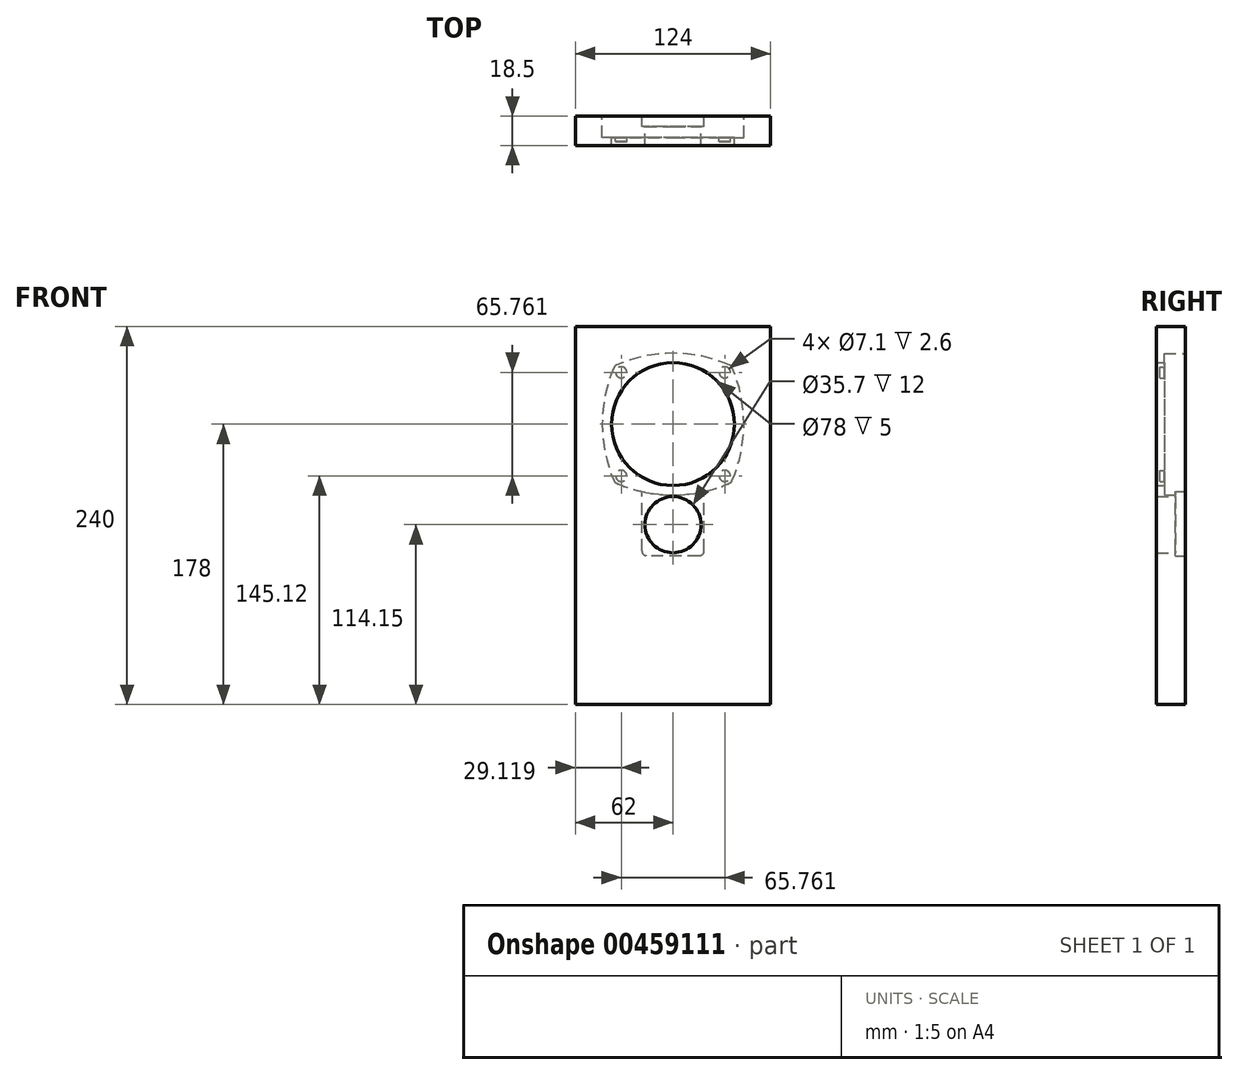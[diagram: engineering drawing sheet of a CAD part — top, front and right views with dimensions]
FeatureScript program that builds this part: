
annotation { "Feature Type Name" : "Feature", "Feature Type Description" : "" }
export const myFeature = defineFeature(function(context is Context, id is Id, definition is map)
    precondition{}
    {
        {
            var Q0;
            Q0=qCreatedBy(makeId("Front.planeOp"),FACE);
            var sketch = newSketch(context, id + "F0", { "sketchPlane" : qUnion([Q0])});
            skLineSegment(sketch, "E0.bottom", {"start": v(0, 0) * mm, "end": v(124, 0) * mm});
            skLineSegment(sketch, "E0.top", {"start": v(0, -240) * mm, "end": v(124, -240) * mm});
            skLineSegment(sketch, "E0.left", {"start": v(0, 0) * mm, "end": v(0, -240) * mm});
            skLineSegment(sketch, "E0.right", {"start": v(124, 0) * mm, "end": v(124, -240) * mm});
            skSolve(sketch);
        }
        {
            var Q0;
            Q0 = qSketchRegion(id + "F0", true);
            extrude(context, id + "F1", {"entities" : qUnion([Q0]), "depth" : 18.5 * mm});
        }
        {
            var Q0;
            Q0=makeQuery(id+"F1.opExtrude","CAP_FACE",FACE,{"disambiguationData":[OSD([sQuery(id+"F0.wireOp",EDGE,"E0.bottom"),sQuery(id+"F0.wireOp",EDGE,"E0.top"),sQuery(id+"F0.wireOp",EDGE,"E0.left"),sQuery(id+"F0.wireOp",EDGE,"E0.right")])],"isStart":true});
            var sketch = newSketch(context, id + "F2", { "sketchPlane" : qUnion([Q0])});
            skCircle(sketch, "E1", {"center": v(-62, -62) * mm, "radius": 39 * mm});
            skLineSegment(sketch, "E2", {"start": v(-62, 0) * mm, "end": v(-62, -240) * mm, "construction": true});
            skCircle(sketch, "E3", {"center": v(-62, -125.85) * mm, "radius": 17.85 * mm});
            skSolve(sketch);
        }
        {
            var Q0;
            Q0 = qSketchRegion(id + "F2", true);
            extrude(context, id + "F3", {"entities" : qUnion([Q0]), "operationType" : NewBodyOperationType.REMOVE, "endBound" : BoundingType.THROUGH_ALL, "oppositeDirection" : true, "depth" : 25.4 * mm});
        }
        {
            var Q0;
            Q0=makeQuery(id+"F2.imprint","IMPRINT",FACE,{"disambiguationData":[TD([[makeQuery(id+"F2.imprint","IMPRINT",EDGE,{"derivedFrom":sQuery(id+"F2.wireOp",EDGE,"E1")}),-1.0]])]});
            var sketch = newSketch(context, id + "F4", { "sketchPlane" : qUnion([Q0])});
            skLineSegment(sketch, "E4", {"start": v(-124, -62) * mm, "end": v(0, -62) * mm, "construction": true});
            skLineSegment(sketch, "E5", {"start": v(0, -62) * mm, "end": v(0, -62) * mm});
            skLineSegment(sketch, "E6.bottom", {"start": v(-107, -17) * mm, "end": v(-17, -17) * mm, "construction": true});
            skLineSegment(sketch, "E6.top", {"start": v(-107, -107) * mm, "end": v(-17, -107) * mm, "construction": true});
            skLineSegment(sketch, "E6.left", {"start": v(-107, -17) * mm, "end": v(-107, -107) * mm, "construction": true});
            skLineSegment(sketch, "E6.right", {"start": v(-17, -17) * mm, "end": v(-17, -107) * mm, "construction": true});
            skArc(sketch, "E7", {"start": v(-24.97, -24.97) * mm, "mid": v(-62, -17) * mm, "end": v(-99.03, -24.97) * mm});
            skArc(sketch, "E8.1.0", {"start": v(-99.03, -24.97) * mm, "mid": v(-107, -62) * mm, "end": v(-99.03, -99.03) * mm});
            skArc(sketch, "E8.2.0", {"start": v(-99.03, -99.03) * mm, "mid": v(-62, -107) * mm, "end": v(-24.97, -99.03) * mm});
            skArc(sketch, "E8.3.0", {"start": v(-24.97, -99.03) * mm, "mid": v(-17, -62) * mm, "end": v(-24.97, -24.97) * mm});
            skPoint(sketch, "E8.center", {"position": v(-62, -62) * mm});
            skSolve(sketch);
        }
        {
            var Q0;
            Q0 = qSketchRegion(id + "F4", true);
            var Q1;
            Q1=sQuery(id+"F4.wireOp",EDGE,"E8.1.0");
            var Q2;
            Q2=sQuery(id+"F4.wireOp",EDGE,"E7");
            var Q3;
            Q3=sQuery(id+"F4.wireOp",EDGE,"E8.3.0");
            var Q4;
            Q4=sQuery(id+"F4.wireOp",EDGE,"E8.2.0");
            extrude(context, id + "F5", {"entities" : qUnion([Q0]), "operationType" : NewBodyOperationType.REMOVE, "surfaceEntities" : qUnion([Q1, Q2, Q3, Q4]), "oppositeDirection" : true, "depth" : 13.5 * mm});
        }
        {
            var Q0;
            Q0=makeQuery(id+"F0.imprint","IMPRINT",FACE,{"disambiguationData":[TD([[makeQuery(id+"F0.imprint","IMPRINT",EDGE,{"derivedFrom":sQuery(id+"F0.wireOp",EDGE,"E0.bottom")}),-1.0]])]});
            cPlane(context, id + "F6", {"entities" : qUnion([Q0]), "cplaneType" : CPlaneType.OFFSET, "offset" : 13.5 * mm, "width" : 150 * mm, "height" : 150 * mm});
        }
        {
            var Q0;
            Q0=qCreatedBy(id+"F6.planeOp",FACE);
            var sketch = newSketch(context, id + "F7", { "sketchPlane" : qUnion([Q0])});
            skCircle(sketch, "E9", {"center": v(62, -62) * mm, "radius": 46.5 * mm, "construction": true});
            skLineSegment(sketch, "E10", {"start": v(62, -62) * mm, "end": v(24.97, -24.97) * mm, "construction": true});
            skCircle(sketch, "E11", {"center": v(29.12, -29.12) * mm, "radius": 3.55 * mm});
            skLineSegment(sketch, "E12.1.0", {"start": v(62, -62) * mm, "end": v(24.97, -99.03) * mm, "construction": true});
            skCircle(sketch, "E12.1.1", {"center": v(29.12, -94.88) * mm, "radius": 3.55 * mm});
            skLineSegment(sketch, "E12.2.0", {"start": v(62, -62) * mm, "end": v(99.03, -99.03) * mm, "construction": true});
            skCircle(sketch, "E12.2.1", {"center": v(94.88, -94.88) * mm, "radius": 3.55 * mm});
            skLineSegment(sketch, "E12.3.0", {"start": v(62, -62) * mm, "end": v(99.03, -24.97) * mm, "construction": true});
            skCircle(sketch, "E12.3.1", {"center": v(94.88, -29.12) * mm, "radius": 3.55 * mm});
            skSolve(sketch);
        }
        {
            var Q0;
            Q0 = qSketchRegion(id + "F7", true);
            extrude(context, id + "F8", {"entities" : qUnion([Q0]), "operationType" : NewBodyOperationType.REMOVE, "depth" : 2.6 * mm});
        }
        {
            var Q0;
            Q0=makeQuery(id+"F2.imprint","IMPRINT",FACE,{"disambiguationData":[TD([[makeQuery(id+"F2.imprint","IMPRINT",EDGE,{"derivedFrom":sQuery(id+"F2.wireOp",EDGE,"E1")}),-1.0]])]});
            var sketch = newSketch(context, id + "F9", { "sketchPlane" : qUnion([Q0])});
            skPoint(sketch, "E13.middle", {"position": v(-62, -125.85) * mm});
            skLineSegment(sketch, "E14.bottom", {"start": v(-81.75, -145.6) * mm, "end": v(-42.25, -145.6) * mm});
            skLineSegment(sketch, "E14.top", {"start": v(-81.75, -102.85) * mm, "end": v(-42.25, -102.85) * mm});
            skLineSegment(sketch, "E14.left", {"start": v(-81.75, -145.6) * mm, "end": v(-81.75, -102.85) * mm});
            skLineSegment(sketch, "E14.right", {"start": v(-42.25, -145.6) * mm, "end": v(-42.25, -102.85) * mm});
            skSolve(sketch);
        }
        {
            var Q0;
            Q0 = qSketchRegion(id + "F9", true);
            extrude(context, id + "F10", {"entities" : qUnion([Q0]), "operationType" : NewBodyOperationType.REMOVE, "oppositeDirection" : true, "depth" : (18.5 - 12) * mm});
        }
        {
            var Q0;
            Q0=makeQuery(id+"F10.boolean.opBoolean","COPY",EDGE,{"derivedFrom":makeQuery(id+"F10.opExtrude","SWEPT_EDGE",EDGE,{"disambiguationData":[OSD([sQuery(id+"F9.wireOp",EDGE,"E14.bottom"),sQuery(id+"F9.wireOp",EDGE,"E14.left")])]})});
            var Q1;
            Q1=makeQuery(id+"F10.boolean.opBoolean","COPY",EDGE,{"derivedFrom":makeQuery(id+"F10.opExtrude","SWEPT_EDGE",EDGE,{"disambiguationData":[OSD([sQuery(id+"F9.wireOp",EDGE,"E14.bottom"),sQuery(id+"F9.wireOp",EDGE,"E14.right")])]})});
            var Q2;
            Q2=makeQuery(id+"F5.boolean.opBoolean","COPY",EDGE,{"derivedFrom":makeQuery(id+"F5.opExtrude","SWEPT_EDGE",EDGE,{"disambiguationData":[OSD([sQuery(id+"F4.wireOp",EDGE,"E8.1.0"),sQuery(id+"F4.wireOp",EDGE,"E8.2.0")])]})});
            var Q3;
            Q3=makeQuery(id+"F5.boolean.opBoolean","COPY",EDGE,{"derivedFrom":makeQuery(id+"F5.opExtrude","SWEPT_EDGE",EDGE,{"disambiguationData":[OSD([sQuery(id+"F4.wireOp",EDGE,"E8.2.0"),sQuery(id+"F4.wireOp",EDGE,"E8.3.0")])]})});
            var Q4;
            Q4=makeQuery(id+"F5.boolean.opBoolean","COPY",EDGE,{"derivedFrom":makeQuery(id+"F5.opExtrude","SWEPT_EDGE",EDGE,{"disambiguationData":[OSD([sQuery(id+"F4.wireOp",EDGE,"E7"),sQuery(id+"F4.wireOp",EDGE,"E8.3.0")])]})});
            var Q5;
            Q5=makeQuery(id+"F5.boolean.opBoolean","COPY",EDGE,{"derivedFrom":makeQuery(id+"F5.opExtrude","SWEPT_EDGE",EDGE,{"disambiguationData":[OSD([sQuery(id+"F4.wireOp",EDGE,"E7"),sQuery(id+"F4.wireOp",EDGE,"E8.1.0")])]})});
            fillet(context, id + "F11", {"entities" : qUnion([Q0, Q1, Q2, Q3, Q4, Q5]), "radius" : 3 * mm, "tangentPropagation" : true, "allowEdgeOverflow" : false});
        }
    });
